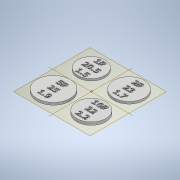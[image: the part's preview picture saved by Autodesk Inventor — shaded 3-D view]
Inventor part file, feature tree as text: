
AUTODESK INVENTOR PART (.ipt)
format: ipt  version: 2020 (Build 240168000, 168)  size: 912,896 bytes
history: native  units: mm
features: other x5, sketch x5, extrude x4
ambient origin geometry x8: Origin, YZ Plane, XZ Plane, XY Plane, X Axis, Y Axis, Z Axis, Center Point
bodies: Body1 (feature_tree)
feature tree (14):
  other  "Твердое тело1"
  sketch  "Эскиз1"
  extrude  "Выдавливание1"  Depth=20.5mm
  extrude  "Выдавливание2"  Depth=23.0mm
  extrude  "Выдавливание3"  Depth=25.0mm
  extrude  "Выдавливание4"  Depth=22.0mm
  other  "Рельеф5"
  other  "Рельеф6"
  other  "Рельеф7"
  other  "Рельеф8"
  sketch  "Эскиз2"
  sketch  "Эскиз3"
  sketch  "Эскиз4"
  sketch  "Эскиз5"
